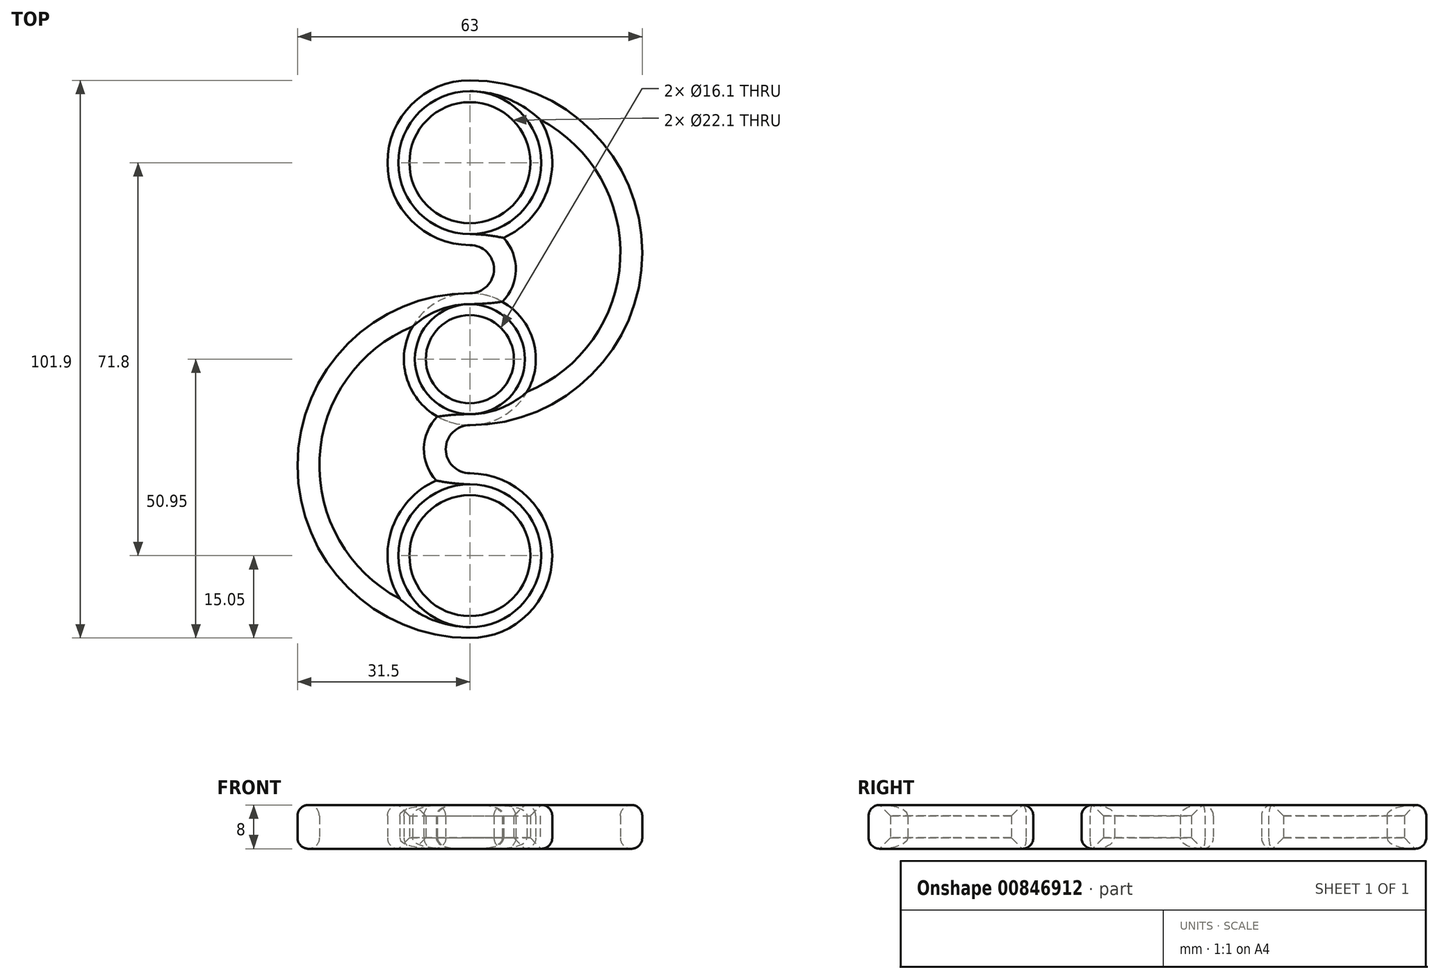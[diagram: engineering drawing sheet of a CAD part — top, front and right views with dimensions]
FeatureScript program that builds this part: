
annotation { "Feature Type Name" : "Feature", "Feature Type Description" : "" }
export const myFeature = defineFeature(function(context is Context, id is Id, definition is map)
    precondition{}
    {
        {
            var Q0;
            Q0=qCreatedBy(makeId("Top.planeOp"),FACE);
            var sketch = newSketch(context, id + "F0", { "sketchPlane" : qUnion([Q0])});
            skCircle(sketch, "E0", {"center": v(0, 0) * mm, "radius": 8.05 * mm});
            skCircle(sketch, "E1", {"center": v(0, 0) * mm, "radius": 12.05 * mm});
            skCircle(sketch, "E2", {"center": v(0, 19.45) * mm, "radius": 31.5 * mm});
            skCircle(sketch, "E3", {"center": v(0, 19.45) * mm, "radius": 27.5 * mm});
            skCircle(sketch, "E4", {"center": v(0, 35.9) * mm, "radius": 11.05 * mm});
            skCircle(sketch, "E5", {"center": v(0, 35.9) * mm, "radius": 15.05 * mm});
            skCircle(sketch, "E6", {"center": v(0, 16.45) * mm, "radius": 4.4 * mm});
            skCircle(sketch, "E7", {"center": v(0, 16.45) * mm, "radius": 8.4 * mm});
            skLineSegment(sketch, "E8", {"start": v(0, 56.29) * mm, "end": v(0, -20.44) * mm, "construction": true});
            skPoint(sketch, "E9", {"position": v(0, 12.05) * mm});
            skPoint(sketch, "E10", {"position": v(0, 8.05) * mm});
            skSolve(sketch);
        }
        {
            var Q0;
            {var subQ0=sQuery(id+"F0.wireOp",EDGE,"E2");var subQ1=sQuery(id+"F0.wireOp",EDGE,"E1");var subQ2=makeQuery(id+"F0.imprint","INTERSECT",VERTEX,{"derivedFrom":[subQ1,subQ0]});Q0=makeQuery(id+"F0.imprint","IMPRINT",FACE,{"disambiguationData":[TD([[makeQuery(id+"F0.imprint","IMPRINT",EDGE,{"disambiguationData":[TD([[subQ2,-1.0]])],"derivedFrom":subQ1}),-1.0]])]});}
            var Q1;
            {var subQ0=sQuery(id+"F0.wireOp",EDGE,"E0");Q1=makeQuery(id+"F0.imprint","IMPRINT",FACE,{"disambiguationData":[TD([[makeQuery(id+"F0.imprint","IMPRINT",EDGE,{"derivedFrom":subQ0}),-1.0]])]});}
            var Q2;
            {var subQ0=sQuery(id+"F0.wireOp",EDGE,"E1");var subQ1=makeQuery(id+"F0.imprint","INTERSECT",VERTEX,{"derivedFrom":[subQ0,sQuery(id+"F0.wireOp",EDGE,"E2")]});Q2=makeQuery(id+"F0.imprint","IMPRINT",FACE,{"disambiguationData":[TD([[makeQuery(id+"F0.imprint","IMPRINT",EDGE,{"disambiguationData":[TD([[subQ1,1.0]])],"derivedFrom":subQ0}),1.0]])]});}
            var Q3;
            {var subQ0=sQuery(id+"F0.wireOp",EDGE,"E3");var subQ1=makeQuery(id+"F0.imprint","INTERSECT",VERTEX,{"derivedFrom":[subQ0,sQuery(id+"F0.wireOp",EDGE,"E4")]});Q3=makeQuery(id+"F0.imprint","IMPRINT",FACE,{"disambiguationData":[TD([[makeQuery(id+"F0.imprint","IMPRINT",EDGE,{"disambiguationData":[TD([[subQ1,1.0]])],"derivedFrom":subQ0}),-1.0]])]});}
            var Q4;
            {var subQ0=sQuery(id+"F0.wireOp",EDGE,"E4");var subQ1=sQuery(id+"F0.wireOp",EDGE,"E3");var subQ2=makeQuery(id+"F0.imprint","INTERSECT",VERTEX,{"derivedFrom":[subQ1,subQ0]});Q4=makeQuery(id+"F0.imprint","IMPRINT",FACE,{"disambiguationData":[TD([[makeQuery(id+"F0.imprint","IMPRINT",EDGE,{"disambiguationData":[TD([[subQ2,1.0]])],"derivedFrom":subQ1}),1.0]])]});}
            var Q5;
            {var subQ0=sQuery(id+"F0.wireOp",EDGE,"E4");var subQ1=sQuery(id+"F0.wireOp",EDGE,"E3");var subQ2=makeQuery(id+"F0.imprint","INTERSECT",VERTEX,{"derivedFrom":[subQ1,subQ0]});Q5=makeQuery(id+"F0.imprint","IMPRINT",FACE,{"disambiguationData":[TD([[makeQuery(id+"F0.imprint","IMPRINT",EDGE,{"disambiguationData":[TD([[subQ2,-1.0]])],"derivedFrom":subQ1}),1.0]])]});}
            var Q6;
            {var subQ0=sQuery(id+"F0.wireOp",EDGE,"E5");var subQ1=makeQuery(id+"F0.imprint","INTERSECT",VERTEX,{"derivedFrom":[subQ0,sQuery(id+"F0.wireOp",EDGE,"r6hCzvR9-9qx0-v0ij-KqBk-qizc1GOy245F")]});Q6=makeQuery(id+"F0.imprint","IMPRINT",FACE,{"disambiguationData":[TD([[makeQuery(id+"F0.imprint","IMPRINT",EDGE,{"disambiguationData":[TD([[subQ1,1.0]])],"derivedFrom":subQ0}),1.0]])]});}
            var Q7;
            {var subQ0=sQuery(id+"F0.wireOp",EDGE,"E6");var subQ1=sQuery(id+"F0.wireOp",EDGE,"E1");var subQ2=makeQuery(id+"F0.imprint","INTERSECT",VERTEX,{"derivedFrom":[subQ1,subQ0]});Q7=makeQuery(id+"F0.imprint","IMPRINT",FACE,{"disambiguationData":[TD([[makeQuery(id+"F0.imprint","IMPRINT",EDGE,{"disambiguationData":[TD([[subQ2,1.0]])],"derivedFrom":subQ1}),-1.0]])]});}
            var Q8;
            {var subQ0=sQuery(id+"F0.wireOp",EDGE,"E1");var subQ1=makeQuery(id+"F0.imprint","INTERSECT",VERTEX,{"derivedFrom":[subQ0,sQuery(id+"F0.wireOp",EDGE,"E6")]});Q8=makeQuery(id+"F0.imprint","IMPRINT",FACE,{"disambiguationData":[TD([[makeQuery(id+"F0.imprint","IMPRINT",EDGE,{"disambiguationData":[TD([[subQ1,1.0]])],"derivedFrom":subQ0}),1.0]])]});}
            extrude(context, id + "F1", {"entities" : qUnion([Q0, Q1, Q2, Q3, Q4, Q5, Q6, Q7, Q8]), "depth" : 8 * mm, "offsetDistance" : 25 * mm});
        }
        {
            var Q0;
            {var subQ0=sQuery(id+"F0.wireOp",EDGE,"E5");Q0=makeQuery(id+"F1.opExtrude","CAP_EDGE",EDGE,{"disambiguationData":[OSD([subQ0]),TDD([makeQuery(id+"F0.imprint","IMPRINT",EDGE,{"disambiguationData":[TD([[makeQuery(id+"F0.imprint","INTERSECT",VERTEX,{"disambiguationData":[OD(0.0)],"derivedFrom":[sQuery(id+"F0.wireOp",EDGE,"E3"),subQ0]}),1.0]])],"derivedFrom":subQ0})])],"isStart":false});}
            var Q1;
            Q1=makeQuery(id+"F1.opExtrude","CAP_EDGE",EDGE,{"disambiguationData":[OSD([sQuery(id+"F0.wireOp",EDGE,"E7")])],"isStart":false});
            var Q2;
            Q2=makeQuery(id+"F1.opExtrude","CAP_EDGE",EDGE,{"disambiguationData":[OSD([sQuery(id+"F0.wireOp",EDGE,"E6")])],"isStart":false});
            var Q3;
            {var subQ0=sQuery(id+"F0.wireOp",EDGE,"E1");Q3=makeQuery(id+"F1.opExtrude","CAP_EDGE",EDGE,{"disambiguationData":[OSD([subQ0]),TDD([makeQuery(id+"F0.imprint","IMPRINT",EDGE,{"disambiguationData":[TD([[makeQuery(id+"F0.imprint","INTERSECT",VERTEX,{"disambiguationData":[OD(0.0)],"derivedFrom":[subQ0,sQuery(id+"F0.wireOp",EDGE,"E7")]}),1.0]])],"derivedFrom":subQ0})])],"isStart":false});}
            var Q4;
            Q4=makeQuery(id+"F1.opExtrude","CAP_EDGE",EDGE,{"disambiguationData":[OSD([sQuery(id+"F0.wireOp",EDGE,"E3")])],"isStart":false});
            var Q5;
            Q5=makeQuery(id+"F1.opExtrude","CAP_EDGE",EDGE,{"disambiguationData":[OSD([sQuery(id+"F0.wireOp",EDGE,"E3")])],"isStart":true});
            var Q6;
            {var subQ0=sQuery(id+"F0.wireOp",EDGE,"E5");var subQ1=makeQuery(id+"F0.imprint","INTERSECT",VERTEX,{"disambiguationData":[OD(0.0)],"derivedFrom":[subQ0,sQuery(id+"F0.wireOp",EDGE,"E7")]});var subQ2=makeQuery(id+"F0.imprint","INTERSECT",VERTEX,{"disambiguationData":[OD(1.0)],"derivedFrom":[sQuery(id+"F0.wireOp",EDGE,"E3"),subQ0]});Q6=makeQuery(id+"F1.opExtrude","CAP_EDGE",EDGE,{"disambiguationData":[OSD([subQ0]),TDD([makeQuery(id+"F0.imprint","IMPRINT",EDGE,{"disambiguationData":[TD([[makeQuery(id+"F0.imprint","INTERSECT",VERTEX,{"derivedFrom":[sQuery(id+"F0.wireOp",EDGE,"E2"),subQ0]}),-1.0]])],"derivedFrom":subQ0}),makeQuery(id+"F0.imprint","IMPRINT",EDGE,{"disambiguationData":[TD([[subQ2,-1.0]])],"derivedFrom":subQ0}),makeQuery(id+"F0.imprint","IMPRINT",EDGE,{"disambiguationData":[TD([[subQ1,-1.0]])],"derivedFrom":subQ0})])],"isStart":true});}
            var Q7;
            Q7=makeQuery(id+"F1.opExtrude","CAP_EDGE",EDGE,{"disambiguationData":[OSD([sQuery(id+"F0.wireOp",EDGE,"E6")])],"isStart":true});
            var Q8;
            {var subQ0=sQuery(id+"F0.wireOp",EDGE,"E5");Q8=makeQuery(id+"F1.opExtrude","CAP_EDGE",EDGE,{"disambiguationData":[OSD([subQ0]),TDD([makeQuery(id+"F0.imprint","IMPRINT",EDGE,{"disambiguationData":[TD([[makeQuery(id+"F0.imprint","INTERSECT",VERTEX,{"disambiguationData":[OD(0.0)],"derivedFrom":[sQuery(id+"F0.wireOp",EDGE,"E3"),subQ0]}),1.0]])],"derivedFrom":subQ0})])],"isStart":true});}
            var Q9;
            Q9=makeQuery(id+"F1.opExtrude","CAP_EDGE",EDGE,{"disambiguationData":[OSD([sQuery(id+"F0.wireOp",EDGE,"E7")])],"isStart":true});
            var Q10;
            {var subQ0=sQuery(id+"F0.wireOp",EDGE,"E1");Q10=makeQuery(id+"F1.opExtrude","CAP_EDGE",EDGE,{"disambiguationData":[OSD([subQ0]),TDD([makeQuery(id+"F0.imprint","IMPRINT",EDGE,{"disambiguationData":[TD([[makeQuery(id+"F0.imprint","INTERSECT",VERTEX,{"disambiguationData":[OD(0.0)],"derivedFrom":[subQ0,sQuery(id+"F0.wireOp",EDGE,"E7")]}),1.0]])],"derivedFrom":subQ0})])],"isStart":true});}
            fillet(context, id + "F2", {"entities" : qUnion([Q0, Q1, Q2, Q3, Q4, Q5, Q6, Q7, Q8, Q9, Q10]), "radius" : 2 * mm, "tangentPropagation" : true, "allowEdgeOverflow" : false});
        }
        {
            var Q0;
            Q0=makeQuery(id+"F1.opExtrude","SWEPT_FACE",FACE,{"disambiguationData":[OSD([sQuery(id+"F0.wireOp",EDGE,"E0")])]});
            var Q1;
            Q1=makeQuery(id+"F1.opExtrude","SWEPT_FACE",FACE,{"disambiguationData":[OSD([sQuery(id+"F0.wireOp",EDGE,"E4")])]});
            chamfer(context, id + "F3", {"entities" : qUnion([Q0, Q1]), "width" : 2 * mm, "tangentPropagation" : true});
        }
        {
            var Q0;
            Q0=makeQuery(id+"F1.opExtrude","SWEPT_BODY",BODY,{"disambiguationData":[OSD([sQuery(id+"F0.wireOp",EDGE,"E0"),sQuery(id+"F0.wireOp",EDGE,"E1"),sQuery(id+"F0.wireOp",EDGE,"61573c0f-0aa0-4bdf-b5a9-0eb16b9a50c6")])]});
            var Q1;
            Q1=makeQuery(id+"F1.opExtrude","SWEPT_FACE",FACE,{"disambiguationData":[OSD([sQuery(id+"F0.wireOp",EDGE,"E0")])]});
            circularPattern(context, id + "F4", {"entities" : qUnion([Q0]), "axis" : qUnion([Q1]), "angle" : 360 * degree, "instanceCount" : 2, "equalSpace" : true});
        }
    });
